# Revit family: Haworth_Janus_Forest_Stool
name_source: partatom
category: Furniture
revit_build: Autodesk Revit 2018 (Build: 20170223_1515(x64)
units: mm (PartAtom-declared; Revit-internal decimal feet)

## family parameters
Always vertical = Yes
Cut with Voids When Loaded = No
OmniClass Number = 23.40.70.14.64.11
OmniClass Title = Office Furniture
Room Calculation Point = No
Shared = No
Work Plane-Based = No

## types (4) — shared parameters
Actual Width = 19"
Assembly Code = E2020200
Foot Rail Finish = Haworth _ Metal _ Stainless Steel
Glide Finish = Haworth _ Polymer _ Slate
Manufacturer = Haworth
Model = HCJC-FO
Note = Verify Final Dim. w/ Haworth
Revision Number = 1
URL = https://www.haworth.com
URL - Product = https://www.haworth.com
Warranty = http://www.haworth.com

## per-type parameters (varying)
| type | Actual Depth | Actual Height | Bar Height | Counter Height | Description | High Back | Low Back | Seat Offset |
| HCCE-FO-S3H - Barstool with High Back | 22" | 46" | Yes | No | Haworth - Forest - Stool - Bar Height - High Back | Yes | No | 5 1/4" |
| HCCE-FO-S3L - Barstool with Low Back | 22" | 38 1/4" | Yes | No | Haworth - Forest - Stool - Bar Height - Low Back | No | Yes | 5 1/4" |
| HCCE-FO-S2H - Counter Stool with High Back | 20 1/2" | 41" | No | Yes | Haworth - Forest - Stool - Counter Height - High Back | Yes | No | 0" |
| HCCE-FO-S2L - Counter Stool with Low Back | 20 1/2" | 33" | No | Yes | Haworth - Forest - Stool - Counter Height - Low Back | No | Yes | 0" |

## geometry (parser evidence)
native form markers: Sweep x11
no freeform markers — native parametric forms only
